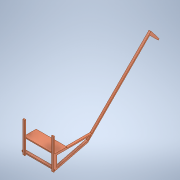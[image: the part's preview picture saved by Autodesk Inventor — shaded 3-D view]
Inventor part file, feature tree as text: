
AUTODESK INVENTOR PART (.ipt)
format: ipt  version: 2021.1 (Build 251245000, 245)  size: 184,320 bytes
history: native  units: in
note: dims shown in document units (in); Inventor stores cm internally (conversion verified against a paired STEP export)
features: extrude x6, sketch x6, plane x1, mirror x1
ambient origin geometry x8: Origin, YZ Plane, XZ Plane, XY Plane, X Axis, Y Axis, Z Axis, Center Point
bodies: Body1 (feature_tree)
feature tree (14):
  extrude  "Extrusion2"  TaperAngle=45.0deg  [1 undecoded]
  extrude  "Extrusion3"  Depth=24.0in
  extrude  "Extrusion4"  Depth=2.0in
  extrude  "Extrusion5"  Depth=4.0in TaperAngle=0.0deg
  extrude  "Extrusion6"  Depth=60.0in TaperAngle=0.0deg
  extrude  "Extrusion7"  Depth=4.0in
  plane  "Work Plane1"
  mirror  "Mirror1"
  sketch  "Sketch1"  dims[d0=179.756in d1=45.0deg]
  sketch  "Sketch2"  dims[d2=2.0in d3=24.0in]
  sketch  "Sketch3"  dims[d4=2.0in d5=15.0in]
  sketch  "Sketch4"  dims[d6=60.0in d9=4.0in d10=0.0in]
  sketch  "Sketch5"  dims[d11=4.0in d12=60.0in d13=0.0in]
  sketch  "Sketch7"  dims[d14=24.0in d15=4.0in d16=4.0in d17=0.0in d18=2.0in d19=4.0in d20=0.0in d21=24.0in d22=2.0in d23=60.0in d24=0.0in d25=4.0in d26=2.0in d27=60.0in d28=0.0in d29=-30.0in]
note: 1 required parameter value undecoded (feature->parameter linkage not recoverable at this tier; creation-order binding heuristic only, values carry confidence <= 0.55)
